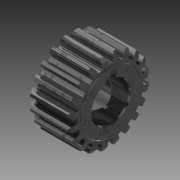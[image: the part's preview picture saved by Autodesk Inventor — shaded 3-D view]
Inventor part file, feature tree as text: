
AUTODESK INVENTOR PART (.ipt)
format: ipt  version: 2014 SP1 (Build 180222100, 222)  size: 366,080 bytes
history: native  units: mm (DEFAULTED — no unit token found)
features: extrude x4, sketch x4, chamfer x3, other x1, fillet x1
ambient origin geometry x8: Origin, YZ Plane, XZ Plane, XY Plane, X Axis, Y Axis, Z Axis, Center Point
bodies: Solid1 (feature_tree)
feature tree (13):
  other  "Gear Blank"
  extrude  "Tooth Profile"  Depth=24.59095mm
  chamfer  "Bore Chamfer Interior"  Distance=12.7mm
  extrude  "Hub"  Depth=3.175mm
  fillet  "Hub Fillet"  Radius=25.4mm
  chamfer  "Bore Chamfer Exterior"  Distance=200.0mm
  chamfer  "Bore Chamfer on Hub"  Distance=3.175mm
  extrude  "Hex Broach"  Depth=3.175mm
  extrude  "Key"  Depth=3.175mm
  sketch  "Sketch2"  dims[d12=90.0deg d24=24.59095mm]
  sketch  "Sketch3"  dims[d26=0.0mm]
  sketch  "Sketch5"  dims[d31=20.32mm]
  sketch  "Sketch16"  dims[d32=0.254mm d77=12.7mm d78=12.7mm d79=25.4mm d83=200.0mm d95=0.381mm d96=3.175mm d97=0.381mm d98=3.175mm d99=0.381mm d100=3.175mm d104=13.97mm d108=30.0deg d109=30.0deg d110=14.224mm d112=0.254mm d117=3.175mm d118=4.7625mm d119=25.4mm d120=0.0mm d121=45.0deg d122=45.0deg d123=45.0deg]
